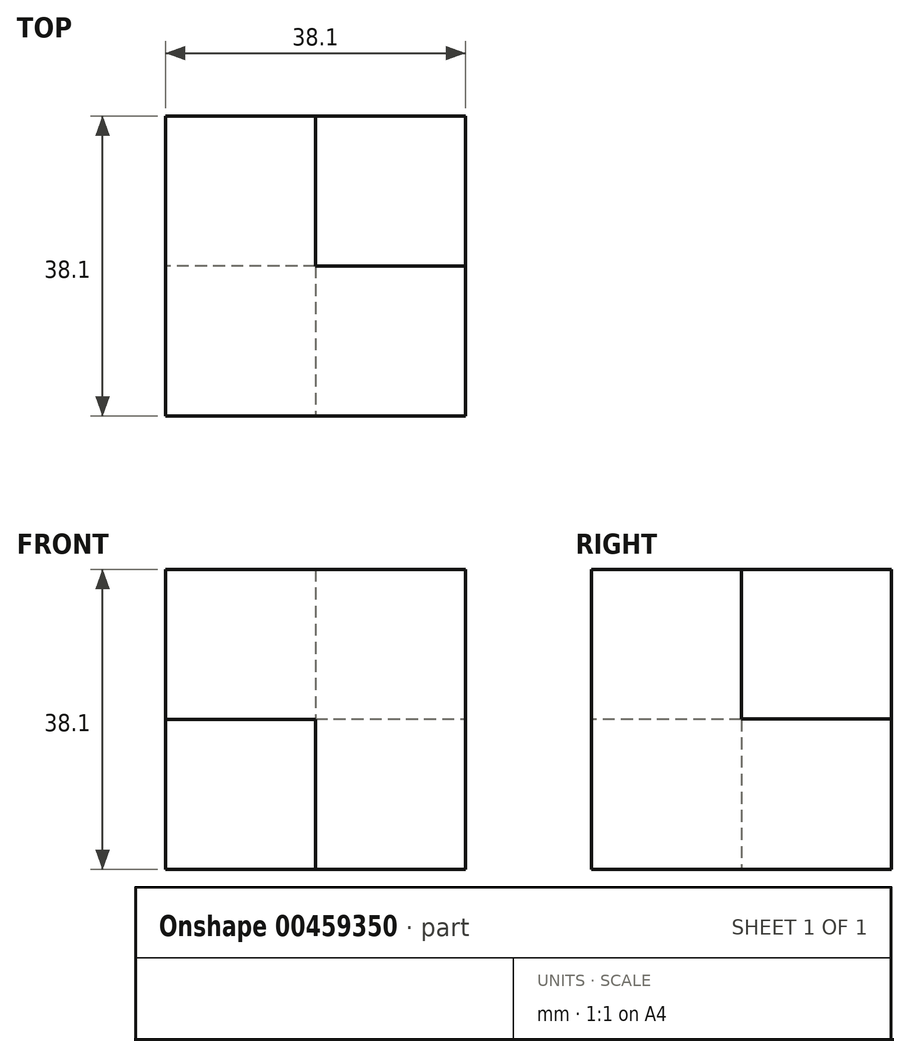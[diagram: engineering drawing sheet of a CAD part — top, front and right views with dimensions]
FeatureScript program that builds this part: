
annotation { "Feature Type Name" : "Feature", "Feature Type Description" : "" }
export const myFeature = defineFeature(function(context is Context, id is Id, definition is map)
    precondition{}
    {
        {
            var Q0;
            Q0=qCreatedBy(makeId("Top.planeOp"),FACE);
            var sketch = newSketch(context, id + "F0", { "sketchPlane" : qUnion([Q0])});
            skLineSegment(sketch, "E0", {"start": v(0, 0) * mm, "end": v(-38.1, 0) * mm});
            skLineSegment(sketch, "E1", {"start": v(-38.1, 0) * mm, "end": v(-38.1, -19.05) * mm});
            skLineSegment(sketch, "E2", {"start": v(-19.05, -19.05) * mm, "end": v(-19.05, -38.1) * mm});
            skLineSegment(sketch, "E3", {"start": v(-19.05, -38.1) * mm, "end": v(0, -38.1) * mm});
            skLineSegment(sketch, "E4", {"start": v(0, -38.1) * mm, "end": v(0, 0) * mm});
            skLineSegment(sketch, "E5", {"start": v(-19.05, -19.05) * mm, "end": v(-19.05, 0) * mm});
            skLineSegment(sketch, "E6", {"start": v(-19.05, 0) * mm, "end": v(-38.1, 0) * mm});
            skPoint(sketch, "E7.startSnap0", {"position": v(-38.1, -9.53) * mm});
            skLineSegment(sketch, "E8", {"start": v(0, -19.05) * mm, "end": v(-19.05, -19.05) * mm});
            skLineSegment(sketch, "E9", {"start": v(-19.05, -19.05) * mm, "end": v(-38.1, -19.05) * mm});
            skSolve(sketch);
        }
        {
            var Q0;
            Q0=makeQuery(id+"F0.imprint","IMPRINT",FACE,{"disambiguationData":[TD([[makeQuery(id+"F0.imprint","IMPRINT",EDGE,{"derivedFrom":sQuery(id+"F0.wireOp",EDGE,"E1")}),1.0]])]});
            var Q1;
            {var subQ0=sQuery(id+"F0.wireOp",EDGE,"E0");Q1=makeQuery(id+"F0.imprint","IMPRINT",FACE,{"disambiguationData":[TD([[makeQuery(id+"F0.imprint","IMPRINT",EDGE,{"derivedFrom":subQ0}),1.0]])]});}
            var Q2;
            Q2=makeQuery(id+"F0.imprint","IMPRINT",FACE,{"disambiguationData":[TD([[makeQuery(id+"F0.imprint","IMPRINT",EDGE,{"derivedFrom":sQuery(id+"F0.wireOp",EDGE,"E2")}),1.0]])]});
            extrude(context, id + "F1", {"entities" : qUnion([Q0, Q1, Q2]), "depth" : 19.1 * mm});
        }
        {
            var Q0;
            Q0=qCreatedBy(makeId("Top.planeOp"),FACE);
            cPlane(context, id + "F2", {"entities" : qUnion([Q0]), "cplaneType" : CPlaneType.OFFSET, "offset" : 19.05 * mm, "width" : 150 * mm, "height" : 150 * mm});
        }
        {
            var Q0;
            Q0=qCreatedBy(id+"F2.planeOp",FACE);
            var sketch = newSketch(context, id + "F3", { "sketchPlane" : qUnion([Q0])});
            skLineSegment(sketch, "E10", {"start": v(-38.1, 0) * mm, "end": v(-38.1, -38.1) * mm});
            skLineSegment(sketch, "E11", {"start": v(-38.1, -38.1) * mm, "end": v(0, -38.1) * mm});
            skLineSegment(sketch, "E12", {"start": v(0, -38.1) * mm, "end": v(0, -19.05) * mm});
            skLineSegment(sketch, "E13", {"start": v(0, -19.05) * mm, "end": v(-19.05, -19.05) * mm});
            skLineSegment(sketch, "E14", {"start": v(-19.05, -19.05) * mm, "end": v(-19.05, 0) * mm});
            skLineSegment(sketch, "E15", {"start": v(-19.05, 0) * mm, "end": v(-38.1, 0) * mm});
            skSolve(sketch);
        }
        {
            var Q0;
            Q0=makeQuery(id+"F3.imprint","IMPRINT",FACE,{"disambiguationData":[TD([[makeQuery(id+"F3.imprint","IMPRINT",EDGE,{"derivedFrom":sQuery(id+"F3.wireOp",EDGE,"E10")}),1.0]])]});
            extrude(context, id + "F4", {"entities" : qUnion([Q0]), "operationType" : NewBodyOperationType.ADD, "depth" : 19.05 * mm});
        }
    });
